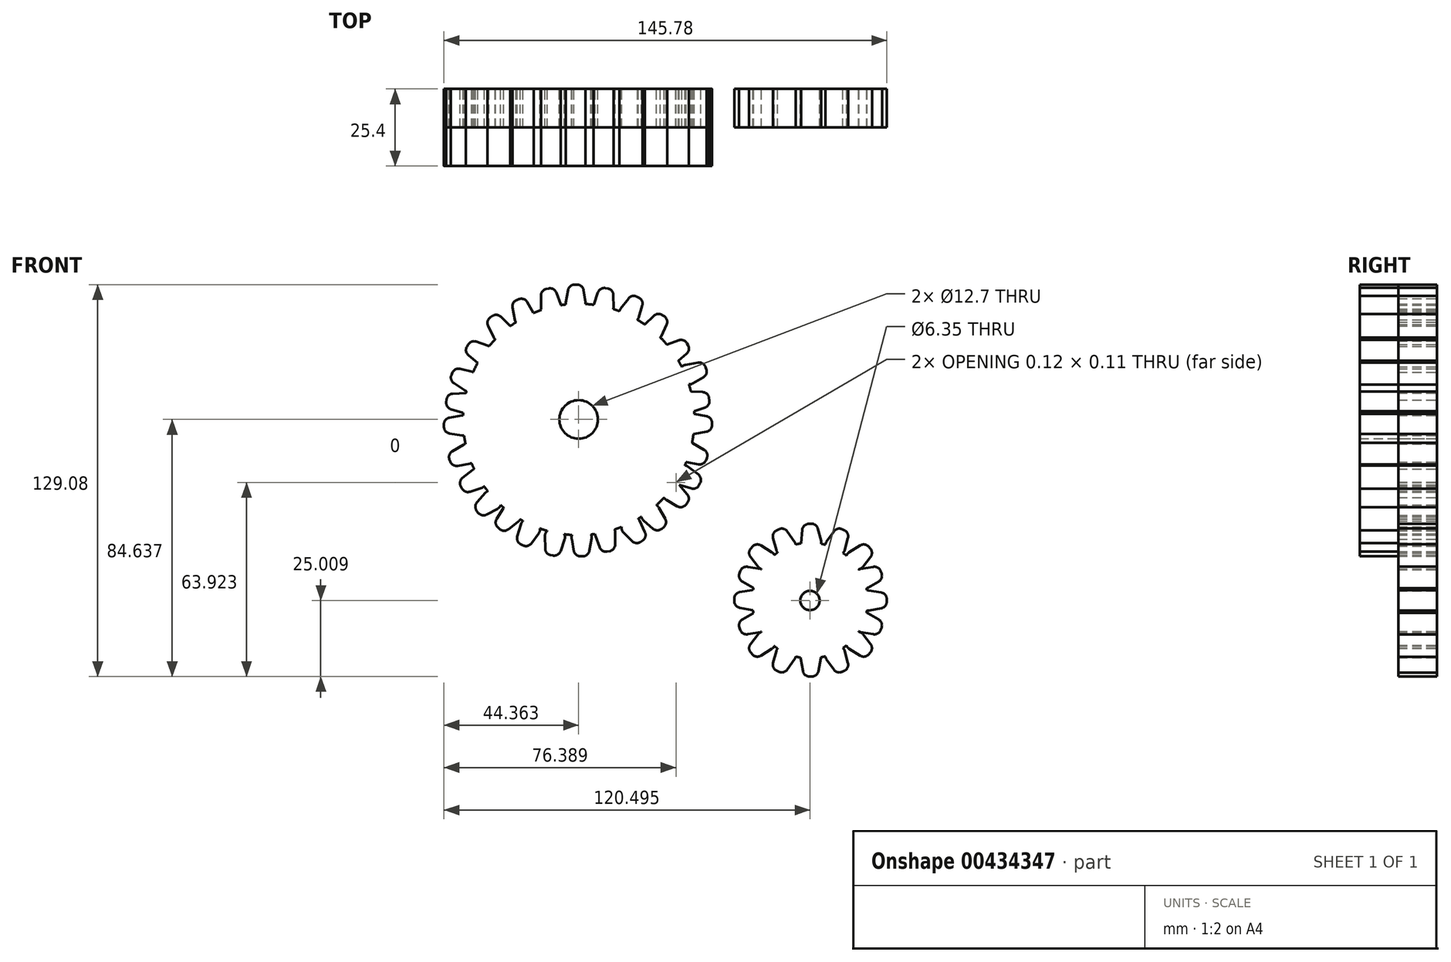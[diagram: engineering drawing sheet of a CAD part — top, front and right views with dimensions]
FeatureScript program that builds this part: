
annotation { "Feature Type Name" : "Feature", "Feature Type Description" : "" }
export const myFeature = defineFeature(function(context is Context, id is Id, definition is map)
    precondition{}
    {
        {
            var Q0;
            Q0=qCreatedBy(makeId("Front.planeOp"),FACE);
            var sketch = newSketch(context, id + "F0", { "sketchPlane" : qUnion([Q0])});
            skCircle(sketch, "E0", {"center": v(-37.42, 28.38) * mm, "radius": 38.1 * mm});
            skCircle(sketch, "E1", {"center": v(-37.42, 28.38) * mm, "radius": 6.35 * mm});
            skCircle(sketch, "E2", {"center": v(38.71, -31.25) * mm, "radius": 19.05 * mm});
            skCircle(sketch, "E3", {"center": v(38.71, -31.25) * mm, "radius": 3.18 * mm});
            skLineSegment(sketch, "E4", {"start": v(-40.93, 71.01) * mm, "end": v(-41.64, 66.96) * mm});
            skLineSegment(sketch, "E5", {"start": v(-38.77, 72.82) * mm, "end": v(-37.94, 72.82) * mm});
            skLineSegment(sketch, "E6", {"start": v(-39.65, 64.59) * mm, "end": v(-37.3, 64.59) * mm});
            skLineSegment(sketch, "E7", {"start": v(-35.15, 67.1) * mm, "end": v(-35.78, 70.98) * mm});
            skArc(sketch, "E8.filletArc", {"start": v(-35.78, 70.98) * mm, "mid": v(-36.52, 72.3) * mm, "end": v(-37.94, 72.82) * mm});
            skArc(sketch, "E9.filletArc", {"start": v(-38.77, 72.82) * mm, "mid": v(-40.18, 72.3) * mm, "end": v(-40.93, 71.01) * mm});
            skArc(sketch, "E10.filletArc", {"start": v(-41.64, 66.96) * mm, "mid": v(-41.2, 65.31) * mm, "end": v(-39.65, 64.59) * mm});
            skArc(sketch, "E11.filletArc", {"start": v(-37.3, 64.59) * mm, "mid": v(-35.64, 65.35) * mm, "end": v(-35.15, 67.1) * mm});
            skLineSegment(sketch, "E12", {"start": v(-31.09, 70.22) * mm, "end": v(-32.46, 66.35) * mm});
            skLineSegment(sketch, "E13", {"start": v(-28.66, 71.65) * mm, "end": v(-27.84, 71.52) * mm});
            skLineSegment(sketch, "E14", {"start": v(-30.88, 63.67) * mm, "end": v(-28.33, 63.25) * mm});
            skLineSegment(sketch, "E15", {"start": v(-25.97, 65.27) * mm, "end": v(-26.01, 69.38) * mm});
            skArc(sketch, "E16.filletArc", {"start": v(-26.01, 69.38) * mm, "mid": v(-26.54, 70.78) * mm, "end": v(-27.84, 71.52) * mm});
            skArc(sketch, "E17.filletArc", {"start": v(-28.66, 71.65) * mm, "mid": v(-30.13, 71.38) * mm, "end": v(-31.09, 70.22) * mm});
            skArc(sketch, "E18.filletArc", {"start": v(-32.46, 66.35) * mm, "mid": v(-32.29, 64.64) * mm, "end": v(-30.88, 63.67) * mm});
            skArc(sketch, "E19.filletArc", {"start": v(-28.33, 63.25) * mm, "mid": v(-26.68, 63.7) * mm, "end": v(-25.97, 65.27) * mm});
            skLineSegment(sketch, "E20", {"start": v(-12.7, 62.53) * mm, "end": v(-15.6, 59.62) * mm});
            skLineSegment(sketch, "E21", {"start": v(-9.9, 62.77) * mm, "end": v(-9.21, 62.3) * mm});
            skLineSegment(sketch, "E22", {"start": v(-15.33, 56.53) * mm, "end": v(-13.22, 55.05) * mm});
            skLineSegment(sketch, "E23", {"start": v(-10.22, 55.85) * mm, "end": v(-8.48, 59.58) * mm});
            skArc(sketch, "E24.filletArc", {"start": v(-8.48, 59.58) * mm, "mid": v(-8.35, 61.07) * mm, "end": v(-9.21, 62.3) * mm});
            skArc(sketch, "E25.filletArc", {"start": v(-9.9, 62.77) * mm, "mid": v(-11.34, 63.16) * mm, "end": v(-12.7, 62.53) * mm});
            skArc(sketch, "E26.filletArc", {"start": v(-15.6, 59.62) * mm, "mid": v(-16.19, 58.01) * mm, "end": v(-15.33, 56.53) * mm});
            skArc(sketch, "E27.filletArc", {"start": v(-13.22, 55.05) * mm, "mid": v(-11.53, 54.75) * mm, "end": v(-10.22, 55.85) * mm});
            skLineSegment(sketch, "E28", {"start": v(-4.46, 54.46) * mm, "end": v(-8.32, 53.05) * mm});
            skLineSegment(sketch, "E29", {"start": v(-1.81, 53.5) * mm, "end": v(-1.4, 52.78) * mm});
            skLineSegment(sketch, "E30", {"start": v(-9.38, 50.14) * mm, "end": v(-8.1, 47.9) * mm});
            skLineSegment(sketch, "E31", {"start": v(-5.04, 47.36) * mm, "end": v(-1.89, 50) * mm});
            skArc(sketch, "E32.filletArc", {"start": v(-1.89, 50) * mm, "mid": v(-1.14, 51.3) * mm, "end": v(-1.4, 52.78) * mm});
            skArc(sketch, "E33.filletArc", {"start": v(-1.81, 53.5) * mm, "mid": v(-2.96, 54.46) * mm, "end": v(-4.46, 54.46) * mm});
            skArc(sketch, "E34.filletArc", {"start": v(-8.32, 53.05) * mm, "mid": v(-9.53, 51.84) * mm, "end": v(-9.38, 50.14) * mm});
            skArc(sketch, "E35.filletArc", {"start": v(-8.1, 47.9) * mm, "mid": v(-6.7, 46.92) * mm, "end": v(-5.04, 47.36) * mm});
            skLineSegment(sketch, "E36", {"start": v(-33.88, -14.86) * mm, "end": v(-33.16, -10.81) * mm});
            skLineSegment(sketch, "E37", {"start": v(-36.03, -16.67) * mm, "end": v(-36.86, -16.67) * mm});
            skLineSegment(sketch, "E38", {"start": v(-35.16, -8.44) * mm, "end": v(-37.74, -8.44) * mm});
            skArc(sketch, "E39.filletArc", {"start": v(-38.95, -15.15) * mm, "mid": v(-38.16, -16.25) * mm, "end": v(-36.86, -16.67) * mm});
            skArc(sketch, "E40.filletArc", {"start": v(-36.03, -16.67) * mm, "mid": v(-34.63, -16.16) * mm, "end": v(-33.88, -14.86) * mm});
            skArc(sketch, "E41.filletArc", {"start": v(-33.16, -10.81) * mm, "mid": v(-33.6, -9.16) * mm, "end": v(-35.16, -8.44) * mm});
            skArc(sketch, "E42.filletArc", {"start": v(-37.74, -8.44) * mm, "mid": v(-39.38, -9.27) * mm, "end": v(-39.67, -11.09) * mm});
            skLineSegment(sketch, "E43", {"start": v(4.66, 29.47) * mm, "end": v(0.45, 30.2) * mm});
            skLineSegment(sketch, "E44", {"start": v(6.47, 27.3) * mm, "end": v(6.47, 26.48) * mm});
            skLineSegment(sketch, "E45", {"start": v(-1.8, 28.32) * mm, "end": v(-1.8, 25.63) * mm});
            skLineSegment(sketch, "E46", {"start": v(0.61, 23.6) * mm, "end": v(4.66, 24.32) * mm});
            skArc(sketch, "E47.filletArc", {"start": v(4.66, 24.32) * mm, "mid": v(5.96, 25.07) * mm, "end": v(6.47, 26.48) * mm});
            skArc(sketch, "E48.filletArc", {"start": v(6.47, 27.3) * mm, "mid": v(5.96, 28.72) * mm, "end": v(4.66, 29.47) * mm});
            skArc(sketch, "E49.filletArc", {"start": v(0.45, 30.2) * mm, "mid": v(-1.11, 29.79) * mm, "end": v(-1.8, 28.32) * mm});
            skArc(sketch, "E50.filletArc", {"start": v(-1.8, 25.63) * mm, "mid": v(-1.06, 24.06) * mm, "end": v(0.61, 23.6) * mm});
            skArc(sketch, "E51.filletArc", {"start": v(-76.25, 28.75) * mm, "mid": v(-76.3, 29.19) * mm, "end": v(-76.43, 29.6) * mm});
            skLineSegment(sketch, "E52", {"start": v(3.4, 37.4) * mm, "end": v(-0.87, 37.55) * mm});
            skLineSegment(sketch, "E53", {"start": v(5.49, 35.51) * mm, "end": v(5.6, 34.7) * mm});
            skLineSegment(sketch, "E54", {"start": v(-2.84, 35.38) * mm, "end": v(-2.47, 32.7) * mm});
            skLineSegment(sketch, "E55", {"start": v(0.2, 31.04) * mm, "end": v(4.1, 32.3) * mm});
            skArc(sketch, "E56.filletArc", {"start": v(4.1, 32.3) * mm, "mid": v(5.29, 33.23) * mm, "end": v(5.6, 34.7) * mm});
            skArc(sketch, "E57.filletArc", {"start": v(5.49, 35.51) * mm, "mid": v(4.78, 36.84) * mm, "end": v(3.4, 37.4) * mm});
            skArc(sketch, "E58.filletArc", {"start": v(-0.87, 37.55) * mm, "mid": v(-2.37, 36.92) * mm, "end": v(-2.84, 35.38) * mm});
            skArc(sketch, "E59.filletArc", {"start": v(-2.47, 32.7) * mm, "mid": v(-1.53, 31.25) * mm, "end": v(0.2, 31.04) * mm});
            skLineSegment(sketch, "E60", {"start": v(3.84, 18.44) * mm, "end": v(0.14, 20.58) * mm});
            skLineSegment(sketch, "E61", {"start": v(4.8, 15.8) * mm, "end": v(4.52, 15.02) * mm});
            skLineSegment(sketch, "E62", {"start": v(-2.62, 19.57) * mm, "end": v(-3.54, 17.04) * mm});
            skLineSegment(sketch, "E63", {"start": v(-1.97, 14.32) * mm, "end": v(2.08, 13.6) * mm});
            skArc(sketch, "E64.filletArc", {"start": v(2.08, 13.6) * mm, "mid": v(3.55, 13.87) * mm, "end": v(4.52, 15.02) * mm});
            skArc(sketch, "E65.filletArc", {"start": v(4.8, 15.8) * mm, "mid": v(4.8, 17.3) * mm, "end": v(3.84, 18.44) * mm});
            skArc(sketch, "E66.filletArc", {"start": v(0.14, 20.58) * mm, "mid": v(-1.48, 20.72) * mm, "end": v(-2.62, 19.57) * mm});
            skArc(sketch, "E67.filletArc", {"start": v(-3.54, 17.04) * mm, "mid": v(-3.4, 15.32) * mm, "end": v(-1.97, 14.32) * mm});
            skLineSegment(sketch, "E68", {"start": v(1.98, 10.22) * mm, "end": v(-1.4, 12.83) * mm});
            skLineSegment(sketch, "E69", {"start": v(2.58, 7.47) * mm, "end": v(2.2, 6.74) * mm});
            skLineSegment(sketch, "E70", {"start": v(-4.28, 12.2) * mm, "end": v(-5.52, 9.81) * mm});
            skLineSegment(sketch, "E71", {"start": v(-4.33, 6.9) * mm, "end": v(-0.4, 5.67) * mm});
            skArc(sketch, "E72.filletArc", {"start": v(-0.4, 5.67) * mm, "mid": v(1.1, 5.73) * mm, "end": v(2.2, 6.74) * mm});
            skArc(sketch, "E73.filletArc", {"start": v(2.58, 7.47) * mm, "mid": v(2.78, 8.96) * mm, "end": v(1.98, 10.22) * mm});
            skArc(sketch, "E74.filletArc", {"start": v(-1.4, 12.83) * mm, "mid": v(-2.99, 13.18) * mm, "end": v(-4.28, 12.2) * mm});
            skArc(sketch, "E75.filletArc", {"start": v(-5.52, 9.81) * mm, "mid": v(-5.6, 8.08) * mm, "end": v(-4.33, 6.9) * mm});
            skLineSegment(sketch, "E76.MirrorCS", {"start": v(-48.45, -14.17) * mm, "end": v(-48.5, -9.9) * mm});
            skArc(sketch, "E77.MirrorCS", {"start": v(-76.23, 6.36) * mm, "mid": v(-76.44, 7.84) * mm, "end": v(-75.66, 9.11) * mm});
            skArc(sketch, "E78.MirrorCS", {"start": v(-70.95, -1.73) * mm, "mid": v(-71.42, -0.3) * mm, "end": v(-70.86, 1.1) * mm});
            skLineSegment(sketch, "E79.MirrorCS", {"start": v(-70.95, -1.73) * mm, "end": v(-70.43, -2.37) * mm});
            skArc(sketch, "E80.MirrorCS", {"start": v(-68.02, 4.28) * mm, "mid": v(-66.54, 4.92) * mm, "end": v(-65.09, 4.2) * mm});
            skArc(sketch, "E81.MirrorCS", {"start": v(-51.3, -6.08) * mm, "mid": v(-50.22, -7.44) * mm, "end": v(-50.57, -9.14) * mm});
            skArc(sketch, "E82.MirrorCS", {"start": v(-73.21, 4.59) * mm, "mid": v(-74.71, 4.63) * mm, "end": v(-75.83, 5.63) * mm});
            skLineSegment(sketch, "E83.MirrorCS", {"start": v(-75.66, 9.11) * mm, "end": v(-72.3, 11.76) * mm});
            skLineSegment(sketch, "E84.MirrorCS", {"start": v(-70.86, 1.1) * mm, "end": v(-68.02, 4.28) * mm});
            skLineSegment(sketch, "E85.MirrorCS", {"start": v(-64.06, -1) * mm, "end": v(-67.68, -2.94) * mm});
            skArc(sketch, "E86.MirrorCS", {"start": v(-56.4, -6.05) * mm, "mid": v(-55.33, -4.83) * mm, "end": v(-53.71, -4.88) * mm});
            skArc(sketch, "E87.MirrorCS", {"start": v(-48.5, -9.9) * mm, "mid": v(-47.84, -8.42) * mm, "end": v(-46.28, -7.99) * mm});
            skLineSegment(sketch, "E88.MirrorCS", {"start": v(-76.23, 6.36) * mm, "end": v(-75.83, 5.63) * mm});
            skLineSegment(sketch, "E89.MirrorCS", {"start": v(-56.5, -12.73) * mm, "end": v(-55.76, -13.1) * mm});
            skLineSegment(sketch, "E90.MirrorCS", {"start": v(-57.62, -10.14) * mm, "end": v(-56.4, -6.05) * mm});
            skLineSegment(sketch, "E91.MirrorCS", {"start": v(-73.17, 13.87) * mm, "end": v(-77.2, 13.1) * mm});
            skArc(sketch, "E92.MirrorCS", {"start": v(-63.42, 2.08) * mm, "mid": v(-63.02, 0.4) * mm, "end": v(-64.06, -1) * mm});
            skLineSegment(sketch, "E93.MirrorCS", {"start": v(-65.09, 4.2) * mm, "end": v(-63.42, 2.08) * mm});
            skLineSegment(sketch, "E94.MirrorCS", {"start": v(-50.57, -9.14) * mm, "end": v(-53.02, -12.44) * mm});
            skLineSegment(sketch, "E95.MirrorCS", {"start": v(-53.71, -4.88) * mm, "end": v(-51.3, -6.08) * mm});
            skArc(sketch, "E96.MirrorCS", {"start": v(-68.15, 8.8) * mm, "mid": v(-68.05, 7.07) * mm, "end": v(-69.31, 5.88) * mm});
            skArc(sketch, "E97.MirrorCS", {"start": v(-72.3, 11.76) * mm, "mid": v(-70.73, 12.14) * mm, "end": v(-69.43, 11.17) * mm});
            skLineSegment(sketch, "E98.MirrorCS", {"start": v(-69.43, 11.17) * mm, "end": v(-68.15, 8.8) * mm});
            skLineSegment(sketch, "E99.MirrorCS", {"start": v(-69.31, 5.88) * mm, "end": v(-73.21, 4.59) * mm});
            skArc(sketch, "E100.MirrorCS", {"start": v(-53.02, -12.44) * mm, "mid": v(-54.27, -13.27) * mm, "end": v(-55.76, -13.1) * mm});
            skLineSegment(sketch, "E101.MirrorCS", {"start": v(-46.28, -7.99) * mm, "end": v(-43.62, -8.42) * mm});
            skArc(sketch, "E102.MirrorCS", {"start": v(-56.5, -12.73) * mm, "mid": v(-57.53, -11.64) * mm, "end": v(-57.62, -10.14) * mm});
            skArc(sketch, "E103.MirrorCS", {"start": v(-67.68, -2.94) * mm, "mid": v(-69.16, -3.16) * mm, "end": v(-70.43, -2.37) * mm});
            skArc(sketch, "E104.MirrorCS", {"start": v(-71.63, 16.6) * mm, "mid": v(-71.76, 14.88) * mm, "end": v(-73.17, 13.87) * mm});
            skLineSegment(sketch, "E105.MirrorCS", {"start": v(-57.05, 68) * mm, "end": v(-57.82, 67.72) * mm});
            skArc(sketch, "E106.MirrorCS", {"start": v(-75.8, 29.72) * mm, "mid": v(-74.23, 29.32) * mm, "end": v(-73.52, 27.87) * mm});
            skLineSegment(sketch, "E107.MirrorCS", {"start": v(-78.95, 43.83) * mm, "end": v(-79.3, 43.08) * mm});
            skArc(sketch, "E108.MirrorCS", {"start": v(-43.62, -8.42) * mm, "mid": v(-42.19, -9.4) * mm, "end": v(-42.02, -11.12) * mm});
            skArc(sketch, "E109.MirrorCS", {"start": v(-79.47, 31.77) * mm, "mid": v(-80.67, 32.68) * mm, "end": v(-81, 34.14) * mm});
            skArc(sketch, "E110.MirrorCS", {"start": v(-47.44, 63.13) * mm, "mid": v(-49.09, 63.57) * mm, "end": v(-49.82, 65.12) * mm});
            skArc(sketch, "E111.MirrorCS", {"start": v(-62.44, 54.73) * mm, "mid": v(-64.12, 54.42) * mm, "end": v(-65.45, 55.5) * mm});
            skLineSegment(sketch, "E112.MirrorCS", {"start": v(-75.55, 30.56) * mm, "end": v(-79.47, 31.77) * mm});
            skLineSegment(sketch, "E113.MirrorCS", {"start": v(-47.21, 71.54) * mm, "end": v(-48.03, 71.39) * mm});
            skLineSegment(sketch, "E114.MirrorCS", {"start": v(-65.87, 62.41) * mm, "end": v(-66.54, 61.93) * mm});
            skArc(sketch, "E115.MirrorCS", {"start": v(-43.37, -15) * mm, "mid": v(-44.32, -16.16) * mm, "end": v(-45.8, -16.44) * mm});
            skArc(sketch, "E116.MirrorCS", {"start": v(-77.2, 13.1) * mm, "mid": v(-78.69, 13.34) * mm, "end": v(-79.66, 14.48) * mm});
            skLineSegment(sketch, "E117.MirrorCS", {"start": v(-46.61, -16.3) * mm, "end": v(-45.8, -16.44) * mm});
            skLineSegment(sketch, "E118.MirrorCS", {"start": v(-73.82, 53.04) * mm, "end": v(-74.23, 52.32) * mm});
            skLineSegment(sketch, "E119.MirrorCS", {"start": v(-81.78, 26.75) * mm, "end": v(-81.77, 25.92) * mm});
            skArc(sketch, "E120.MirrorCS", {"start": v(-49.83, 69.23) * mm, "mid": v(-49.32, 70.64) * mm, "end": v(-48.03, 71.39) * mm});
            skArc(sketch, "E121.MirrorCS", {"start": v(-67.23, 59.2) * mm, "mid": v(-67.38, 60.7) * mm, "end": v(-66.54, 61.93) * mm});
            skArc(sketch, "E122.MirrorCS", {"start": v(-74.56, 37.09) * mm, "mid": v(-73.06, 36.47) * mm, "end": v(-72.57, 34.93) * mm});
            skArc(sketch, "E123.MirrorCS", {"start": v(-65.87, 62.41) * mm, "mid": v(-64.42, 62.82) * mm, "end": v(-63.06, 62.2) * mm});
            skLineSegment(sketch, "E124.MirrorCS", {"start": v(-72.57, 34.93) * mm, "end": v(-72.9, 32.26) * mm});
            skArc(sketch, "E125.MirrorCS", {"start": v(-46.61, -16.3) * mm, "mid": v(-47.92, -15.57) * mm, "end": v(-48.45, -14.17) * mm});
            skLineSegment(sketch, "E126.MirrorCS", {"start": v(-71, 41.36) * mm, "end": v(-72.1, 38.9) * mm});
            skLineSegment(sketch, "E127.MirrorCS", {"start": v(-73.52, 27.87) * mm, "end": v(-73.49, 25.17) * mm});
            skLineSegment(sketch, "E128.MirrorCS", {"start": v(-66.21, 49.78) * mm, "end": v(-67.47, 47.52) * mm});
            skLineSegment(sketch, "E129.MirrorCS", {"start": v(-53.31, 60.62) * mm, "end": v(-55.73, 59.7) * mm});
            skArc(sketch, "E130.MirrorCS", {"start": v(-72.9, 32.26) * mm, "mid": v(-73.83, 30.8) * mm, "end": v(-75.55, 30.56) * mm});
            skLineSegment(sketch, "E131.MirrorCS", {"start": v(-75.87, 23.12) * mm, "end": v(-79.93, 23.78) * mm});
            skLineSegment(sketch, "E132.MirrorCS", {"start": v(-70.52, 46.95) * mm, "end": v(-73.7, 49.55) * mm});
            skArc(sketch, "E133.MirrorCS", {"start": v(-60.11, 59.34) * mm, "mid": v(-59.5, 57.74) * mm, "end": v(-60.34, 56.24) * mm});
            skLineSegment(sketch, "E134.MirrorCS", {"start": v(-58.44, 61.22) * mm, "end": v(-59.2, 65.26) * mm});
            skLineSegment(sketch, "E135.MirrorCS", {"start": v(-75.13, 38.05) * mm, "end": v(-78.53, 40.37) * mm});
            skArc(sketch, "E136.MirrorCS", {"start": v(-67.3, 52.68) * mm, "mid": v(-66.08, 51.48) * mm, "end": v(-66.21, 49.78) * mm});
            skArc(sketch, "E137.MirrorCS", {"start": v(-52.29, 63.55) * mm, "mid": v(-52.12, 61.84) * mm, "end": v(-53.31, 60.62) * mm});
            skLineSegment(sketch, "E138.MirrorCS", {"start": v(-72.58, 19.13) * mm, "end": v(-71.63, 16.6) * mm});
            skLineSegment(sketch, "E139.MirrorCS", {"start": v(-65.45, 55.5) * mm, "end": v(-67.23, 59.2) * mm});
            skArc(sketch, "E140.MirrorCS", {"start": v(-43.35, 66.28) * mm, "mid": v(-43.5, 64.57) * mm, "end": v(-44.9, 63.58) * mm});
            skArc(sketch, "E141.MirrorCS", {"start": v(-73.82, 53.04) * mm, "mid": v(-72.69, 54.02) * mm, "end": v(-71.19, 54.03) * mm});
            skLineSegment(sketch, "E142.MirrorCS", {"start": v(-49.82, 65.12) * mm, "end": v(-49.83, 69.23) * mm});
            skArc(sketch, "E143.MirrorCS", {"start": v(-73.7, 49.55) * mm, "mid": v(-74.47, 50.84) * mm, "end": v(-74.23, 52.32) * mm});
            skArc(sketch, "E144.MirrorCS", {"start": v(-57.05, 68) * mm, "mid": v(-55.55, 68.03) * mm, "end": v(-54.39, 67.08) * mm});
            skArc(sketch, "E145.MirrorCS", {"start": v(-81.78, 26.75) * mm, "mid": v(-81.28, 28.16) * mm, "end": v(-80, 28.93) * mm});
            skArc(sketch, "E146.MirrorCS", {"start": v(-55.73, 59.7) * mm, "mid": v(-57.44, 59.83) * mm, "end": v(-58.44, 61.22) * mm});
            skArc(sketch, "E147.MirrorCS", {"start": v(-80.9, 34.96) * mm, "mid": v(-80.2, 36.3) * mm, "end": v(-78.83, 36.88) * mm});
            skLineSegment(sketch, "E148.MirrorCS", {"start": v(-80, 28.93) * mm, "end": v(-75.8, 29.72) * mm});
            skLineSegment(sketch, "E149.MirrorCS", {"start": v(-76.41, 45.06) * mm, "end": v(-72.27, 44) * mm});
            skArc(sketch, "E150.MirrorCS", {"start": v(-72.27, 44) * mm, "mid": v(-71.02, 42.98) * mm, "end": v(-71, 41.36) * mm});
            skArc(sketch, "E151.MirrorCS", {"start": v(-79.93, 23.78) * mm, "mid": v(-81.23, 24.52) * mm, "end": v(-81.77, 25.92) * mm});
            skLineSegment(sketch, "E152.MirrorCS", {"start": v(-44.9, 63.58) * mm, "end": v(-47.44, 63.13) * mm});
            skArc(sketch, "E153.MirrorCS", {"start": v(-78.53, 40.37) * mm, "mid": v(-79.4, 41.58) * mm, "end": v(-79.3, 43.08) * mm});
            skLineSegment(sketch, "E154.MirrorCS", {"start": v(-44.77, 70.13) * mm, "end": v(-43.35, 66.28) * mm});
            skLineSegment(sketch, "E155.MirrorCS", {"start": v(-60.34, 56.24) * mm, "end": v(-62.44, 54.73) * mm});
            skArc(sketch, "E156.MirrorCS", {"start": v(-79.96, 15.25) * mm, "mid": v(-79.98, 16.75) * mm, "end": v(-79.03, 17.91) * mm});
            skLineSegment(sketch, "E157.MirrorCS", {"start": v(-79.96, 15.25) * mm, "end": v(-79.66, 14.48) * mm});
            skLineSegment(sketch, "E158.MirrorCS", {"start": v(-78.83, 36.88) * mm, "end": v(-74.56, 37.09) * mm});
            skLineSegment(sketch, "E159.MirrorCS", {"start": v(-63.06, 62.2) * mm, "end": v(-60.11, 59.34) * mm});
            skLineSegment(sketch, "E160.MirrorCS", {"start": v(-79.03, 17.91) * mm, "end": v(-75.35, 20.1) * mm});
            skArc(sketch, "E161.MirrorCS", {"start": v(-67.47, 47.52) * mm, "mid": v(-68.86, 46.52) * mm, "end": v(-70.52, 46.95) * mm});
            skLineSegment(sketch, "E162.MirrorCS", {"start": v(-80.9, 34.96) * mm, "end": v(-81, 34.14) * mm});
            skArc(sketch, "E163.MirrorCS", {"start": v(-47.21, 71.54) * mm, "mid": v(-45.73, 71.28) * mm, "end": v(-44.77, 70.13) * mm});
            skLineSegment(sketch, "E164.MirrorCS", {"start": v(-42.02, -11.12) * mm, "end": v(-43.37, -15) * mm});
            skArc(sketch, "E165.MirrorCS", {"start": v(-75.35, 20.1) * mm, "mid": v(-73.74, 20.26) * mm, "end": v(-72.58, 19.13) * mm});
            skArc(sketch, "E166.MirrorCS", {"start": v(-78.95, 43.83) * mm, "mid": v(-77.9, 44.9) * mm, "end": v(-76.41, 45.06) * mm});
            skArc(sketch, "E167.MirrorCS", {"start": v(-73.49, 25.17) * mm, "mid": v(-74.2, 23.6) * mm, "end": v(-75.87, 23.12) * mm});
            skLineSegment(sketch, "E168.MirrorCS", {"start": v(-71.19, 54.03) * mm, "end": v(-67.3, 52.68) * mm});
            skLineSegment(sketch, "E169.MirrorCS", {"start": v(-54.39, 67.08) * mm, "end": v(-52.29, 63.55) * mm});
            skArc(sketch, "E170.MirrorCS", {"start": v(-72.1, 38.9) * mm, "mid": v(-73.42, 37.77) * mm, "end": v(-75.13, 38.05) * mm});
            skArc(sketch, "E171.MirrorCS", {"start": v(-59.2, 65.26) * mm, "mid": v(-58.96, 66.74) * mm, "end": v(-57.82, 67.72) * mm});
            skLineSegment(sketch, "E172", {"start": v(-15.6, -8.72) * mm, "end": v(-17.4, -4.85) * mm});
            skLineSegment(sketch, "E173", {"start": v(-16.32, -11.45) * mm, "end": v(-17, -11.92) * mm});
            skLineSegment(sketch, "E174", {"start": v(-20.23, -4.1) * mm, "end": v(-22.44, -5.64) * mm});
            skLineSegment(sketch, "E175", {"start": v(-22.71, -8.77) * mm, "end": v(-19.8, -11.67) * mm});
            skArc(sketch, "E176.filletArc", {"start": v(-19.8, -11.67) * mm, "mid": v(-18.45, -12.3) * mm, "end": v(-17, -11.92) * mm});
            skArc(sketch, "E177.filletArc", {"start": v(-16.32, -11.45) * mm, "mid": v(-15.46, -10.22) * mm, "end": v(-15.6, -8.72) * mm});
            skArc(sketch, "E178.filletArc", {"start": v(-17.4, -4.85) * mm, "mid": v(-18.64, -3.81) * mm, "end": v(-20.23, -4.1) * mm});
            skArc(sketch, "E179.filletArc", {"start": v(-22.44, -5.64) * mm, "mid": v(-23.3, -7.14) * mm, "end": v(-22.71, -8.77) * mm});
            skLineSegment(sketch, "E180", {"start": v(1.86, 47.1) * mm, "end": v(-2.35, 46.35) * mm});
            skLineSegment(sketch, "E181", {"start": v(4.3, 45.68) * mm, "end": v(4.58, 44.9) * mm});
            skLineSegment(sketch, "E182", {"start": v(-3.82, 43.8) * mm, "end": v(-2.9, 41.28) * mm});
            skLineSegment(sketch, "E183", {"start": v(0.06, 40.2) * mm, "end": v(3.62, 42.26) * mm});
            skArc(sketch, "E184.filletArc", {"start": v(3.62, 42.26) * mm, "mid": v(4.58, 43.4) * mm, "end": v(4.58, 44.9) * mm});
            skArc(sketch, "E185.filletArc", {"start": v(4.3, 45.68) * mm, "mid": v(3.33, 46.83) * mm, "end": v(1.86, 47.1) * mm});
            skArc(sketch, "E186.filletArc", {"start": v(-2.35, 46.35) * mm, "mid": v(-3.68, 45.42) * mm, "end": v(-3.82, 43.8) * mm});
            skArc(sketch, "E187.filletArc", {"start": v(-2.9, 41.28) * mm, "mid": v(-1.67, 40.05) * mm, "end": v(0.06, 40.2) * mm});
            skLineSegment(sketch, "E188", {"start": v(-1.66, 3.73) * mm, "end": v(-4.4, 7) * mm});
            skLineSegment(sketch, "E189", {"start": v(-1.66, 0.91) * mm, "end": v(-2.19, 0.28) * mm});
            skLineSegment(sketch, "E190", {"start": v(-7.34, 7) * mm, "end": v(-9.07, 4.94) * mm});
            skLineSegment(sketch, "E191", {"start": v(-8.52, 1.84) * mm, "end": v(-4.96, -0.21) * mm});
            skArc(sketch, "E192.filletArc", {"start": v(-4.96, -0.21) * mm, "mid": v(-3.49, -0.47) * mm, "end": v(-2.19, 0.28) * mm});
            skArc(sketch, "E193.filletArc", {"start": v(-1.66, 0.91) * mm, "mid": v(-1.14, 2.32) * mm, "end": v(-1.66, 3.73) * mm});
            skArc(sketch, "E194.filletArc", {"start": v(-4.4, 7) * mm, "mid": v(-5.87, 7.69) * mm, "end": v(-7.34, 7) * mm});
            skArc(sketch, "E195.filletArc", {"start": v(-9.07, 4.94) * mm, "mid": v(-9.52, 3.27) * mm, "end": v(-8.52, 1.84) * mm});
            skLineSegment(sketch, "E196", {"start": v(-8.95, -4.3) * mm, "end": v(-11.07, -0.6) * mm});
            skLineSegment(sketch, "E197", {"start": v(-9.46, -7.08) * mm, "end": v(-10.1, -7.6) * mm});
            skLineSegment(sketch, "E198", {"start": v(-13.95, -0.07) * mm, "end": v(-16.03, -1.79) * mm});
            skLineSegment(sketch, "E199", {"start": v(-16.04, -4.93) * mm, "end": v(-12.91, -7.6) * mm});
            skArc(sketch, "E200.filletArc", {"start": v(-12.91, -7.6) * mm, "mid": v(-11.5, -8.11) * mm, "end": v(-10.1, -7.6) * mm});
            skArc(sketch, "E201.filletArc", {"start": v(-9.46, -7.08) * mm, "mid": v(-8.7, -5.79) * mm, "end": v(-8.95, -4.3) * mm});
            skArc(sketch, "E202.filletArc", {"start": v(-11.07, -0.6) * mm, "mid": v(-12.39, 0.34) * mm, "end": v(-13.95, -0.07) * mm});
            skArc(sketch, "E203.filletArc", {"start": v(-16.03, -1.79) * mm, "mid": v(-16.77, -3.36) * mm, "end": v(-16.04, -4.93) * mm});
            skLineSegment(sketch, "E204", {"start": v(-25.43, -12.84) * mm, "end": v(-25.43, -8.56) * mm});
            skLineSegment(sketch, "E205", {"start": v(-27.24, -15) * mm, "end": v(-28.06, -15.14) * mm});
            skLineSegment(sketch, "E206", {"start": v(-27.68, -6.68) * mm, "end": v(-30.33, -7.14) * mm});
            skLineSegment(sketch, "E207", {"start": v(-31.9, -9.87) * mm, "end": v(-30.5, -13.73) * mm});
            skArc(sketch, "E208.filletArc", {"start": v(-30.5, -13.73) * mm, "mid": v(-29.53, -14.88) * mm, "end": v(-28.06, -15.14) * mm});
            skArc(sketch, "E209.filletArc", {"start": v(-27.24, -15) * mm, "mid": v(-25.95, -14.24) * mm, "end": v(-25.43, -12.84) * mm});
            skArc(sketch, "E210.filletArc", {"start": v(-25.43, -8.56) * mm, "mid": v(-26.12, -7.1) * mm, "end": v(-27.68, -6.68) * mm});
            skArc(sketch, "E211.filletArc", {"start": v(-30.33, -7.14) * mm, "mid": v(-31.75, -8.14) * mm, "end": v(-31.9, -9.87) * mm});
            skLineSegment(sketch, "E212", {"start": v(-38.95, -15.15) * mm, "end": v(-39.67, -11.09) * mm});
            skLineSegment(sketch, "E213", {"start": v(-60.59, -7.83) * mm, "end": v(-57.22, -5.2) * mm});
            skLineSegment(sketch, "E214", {"start": v(-63.4, -7.73) * mm, "end": v(-64.02, -7.18) * mm});
            skLineSegment(sketch, "E215", {"start": v(-57.11, -2.27) * mm, "end": v(-59.11, -0.47) * mm});
            skLineSegment(sketch, "E216", {"start": v(-62.23, -0.9) * mm, "end": v(-64.4, -4.39) * mm});
            skArc(sketch, "E217.filletArc", {"start": v(-64.4, -4.39) * mm, "mid": v(-64.72, -5.85) * mm, "end": v(-64.02, -7.18) * mm});
            skArc(sketch, "E218.filletArc", {"start": v(-63.4, -7.73) * mm, "mid": v(-62.01, -8.3) * mm, "end": v(-60.59, -7.83) * mm});
            skArc(sketch, "E219.filletArc", {"start": v(-57.22, -5.2) * mm, "mid": v(-56.48, -3.76) * mm, "end": v(-57.11, -2.27) * mm});
            skArc(sketch, "E220.filletArc", {"start": v(-59.11, -0.47) * mm, "mid": v(-60.77, 0.04) * mm, "end": v(-62.23, -0.9) * mm});
            skLineSegment(sketch, "E221", {"start": v(67.67, -31.25) * mm, "end": v(13.37, -31.25) * mm});
            skLineSegment(sketch, "E222", {"start": v(46.57, -8.5) * mm, "end": v(44.12, -12) * mm});
            skLineSegment(sketch, "E223", {"start": v(49.29, -7.76) * mm, "end": v(50.04, -8.11) * mm});
            skLineSegment(sketch, "E224", {"start": v(44.87, -14.83) * mm, "end": v(47.31, -15.97) * mm});
            skLineSegment(sketch, "E225", {"start": v(50.16, -14.64) * mm, "end": v(51.23, -10.67) * mm});
            skArc(sketch, "E226.filletArc", {"start": v(51.23, -10.67) * mm, "mid": v(51.1, -9.17) * mm, "end": v(50.04, -8.11) * mm});
            skArc(sketch, "E227.filletArc", {"start": v(49.29, -7.76) * mm, "mid": v(47.8, -7.63) * mm, "end": v(46.57, -8.5) * mm});
            skArc(sketch, "E228.filletArc", {"start": v(44.12, -12) * mm, "mid": v(43.83, -13.59) * mm, "end": v(44.87, -14.83) * mm});
            skArc(sketch, "E229.filletArc", {"start": v(47.31, -15.97) * mm, "mid": v(49.05, -15.97) * mm, "end": v(50.16, -14.64) * mm});
            skLineSegment(sketch, "E230", {"start": v(55.2, -13.1) * mm, "end": v(51.59, -15.36) * mm});
            skLineSegment(sketch, "E231", {"start": v(58, -13.49) * mm, "end": v(58.55, -14.1) * mm});
            skLineSegment(sketch, "E232", {"start": v(51.18, -18.27) * mm, "end": v(52.98, -20.27) * mm});
            skLineSegment(sketch, "E233", {"start": v(56.12, -20.16) * mm, "end": v(58.65, -16.92) * mm});
            skArc(sketch, "E234.filletArc", {"start": v(58.65, -16.92) * mm, "mid": v(59.12, -15.5) * mm, "end": v(58.55, -14.1) * mm});
            skArc(sketch, "E235.filletArc", {"start": v(58, -13.49) * mm, "mid": v(56.68, -12.79) * mm, "end": v(55.2, -13.1) * mm});
            skArc(sketch, "E236.filletArc", {"start": v(51.59, -15.36) * mm, "mid": v(50.7, -16.72) * mm, "end": v(51.18, -18.27) * mm});
            skArc(sketch, "E237.filletArc", {"start": v(52.98, -20.27) * mm, "mid": v(54.58, -20.95) * mm, "end": v(56.12, -20.16) * mm});
            skLineSegment(sketch, "E238", {"start": v(35.3, -12.51) * mm, "end": v(35.27, -12.66) * mm});
            skArc(sketch, "E239.filletArc", {"start": v(38.9, -6.67) * mm, "mid": v(38.87, -6.67) * mm, "end": v(38.83, -6.67) * mm});
            skLineSegment(sketch, "E240", {"start": v(59.57, -20.14) * mm, "end": v(55.36, -20.88) * mm});
            skLineSegment(sketch, "E241", {"start": v(62, -21.55) * mm, "end": v(62.29, -22.33) * mm});
            skLineSegment(sketch, "E242", {"start": v(53.9, -23.43) * mm, "end": v(54.81, -25.95) * mm});
            skLineSegment(sketch, "E243", {"start": v(57.77, -27.03) * mm, "end": v(61.33, -24.98) * mm});
            skArc(sketch, "E244.filletArc", {"start": v(61.33, -24.98) * mm, "mid": v(62.29, -23.83) * mm, "end": v(62.29, -22.33) * mm});
            skArc(sketch, "E245.filletArc", {"start": v(62, -21.55) * mm, "mid": v(61.04, -20.4) * mm, "end": v(59.57, -20.14) * mm});
            skArc(sketch, "E246.filletArc", {"start": v(55.36, -20.88) * mm, "mid": v(54.03, -21.81) * mm, "end": v(53.9, -23.43) * mm});
            skArc(sketch, "E247.filletArc", {"start": v(54.81, -25.95) * mm, "mid": v(56.04, -27.18) * mm, "end": v(57.77, -27.03) * mm});
            skLineSegment(sketch, "E248.MirrorCS", {"start": v(19.8, -13.49) * mm, "end": v(19.25, -14.1) * mm});
            skLineSegment(sketch, "E249.MirrorCS", {"start": v(15.8, -21.55) * mm, "end": v(15.51, -22.33) * mm});
            skLineSegment(sketch, "E250.MirrorCS", {"start": v(26.62, -18.27) * mm, "end": v(24.82, -20.27) * mm});
            skLineSegment(sketch, "E251.MirrorCS", {"start": v(23.91, -23.43) * mm, "end": v(22.99, -25.95) * mm});
            skArc(sketch, "E252.MirrorCS", {"start": v(22.99, -25.95) * mm, "mid": v(21.76, -27.18) * mm, "end": v(20.04, -27.03) * mm});
            skArc(sketch, "E253.MirrorCS", {"start": v(19.15, -16.92) * mm, "mid": v(18.69, -15.5) * mm, "end": v(19.25, -14.1) * mm});
            skArc(sketch, "E254.MirrorCS", {"start": v(16.48, -24.98) * mm, "mid": v(15.51, -23.83) * mm, "end": v(15.51, -22.33) * mm});
            skArc(sketch, "E255.MirrorCS", {"start": v(26.21, -15.36) * mm, "mid": v(27.1, -16.72) * mm, "end": v(26.62, -18.27) * mm});
            skLineSegment(sketch, "E256.MirrorCS", {"start": v(28.52, -7.76) * mm, "end": v(27.76, -8.11) * mm});
            skLineSegment(sketch, "E257.MirrorCS", {"start": v(32.93, -14.83) * mm, "end": v(30.49, -15.97) * mm});
            skLineSegment(sketch, "E258.MirrorCS", {"start": v(21.68, -20.16) * mm, "end": v(19.15, -16.92) * mm});
            skLineSegment(sketch, "E259.MirrorCS", {"start": v(20.04, -27.03) * mm, "end": v(16.48, -24.98) * mm});
            skArc(sketch, "E260.MirrorCS", {"start": v(24.82, -20.27) * mm, "mid": v(23.22, -20.95) * mm, "end": v(21.68, -20.16) * mm});
            skArc(sketch, "E261.MirrorCS", {"start": v(19.8, -13.49) * mm, "mid": v(21.13, -12.79) * mm, "end": v(22.6, -13.1) * mm});
            skArc(sketch, "E262.MirrorCS", {"start": v(15.8, -21.55) * mm, "mid": v(16.76, -20.4) * mm, "end": v(18.24, -20.14) * mm});
            skArc(sketch, "E263.MirrorCS", {"start": v(22.44, -20.88) * mm, "mid": v(23.77, -21.81) * mm, "end": v(23.91, -23.43) * mm});
            skLineSegment(sketch, "E264.MirrorCS", {"start": v(27.64, -14.64) * mm, "end": v(26.57, -10.67) * mm});
            skArc(sketch, "E265.MirrorCS", {"start": v(26.57, -10.67) * mm, "mid": v(26.7, -9.17) * mm, "end": v(27.76, -8.11) * mm});
            skArc(sketch, "E266.MirrorCS", {"start": v(28.52, -7.76) * mm, "mid": v(30, -7.63) * mm, "end": v(31.24, -8.5) * mm});
            skArc(sketch, "E267.MirrorCS", {"start": v(30.49, -15.97) * mm, "mid": v(28.75, -15.97) * mm, "end": v(27.64, -14.64) * mm});
            skLineSegment(sketch, "E268.MirrorCS", {"start": v(18.24, -20.14) * mm, "end": v(22.44, -20.88) * mm});
            skLineSegment(sketch, "E269.MirrorCS", {"start": v(22.6, -13.1) * mm, "end": v(26.21, -15.36) * mm});
            skLineSegment(sketch, "E270.MirrorCS", {"start": v(31.24, -8.5) * mm, "end": v(33.69, -12) * mm});
            skArc(sketch, "E271.MirrorCS", {"start": v(33.69, -12) * mm, "mid": v(33.97, -13.59) * mm, "end": v(32.93, -14.83) * mm});
            skLineSegment(sketch, "E272.MirrorCS", {"start": v(38.9, -15.06) * mm, "end": v(38.25, -15.06) * mm});
            skArc(sketch, "E273.MirrorCS", {"start": v(38.9, -6.67) * mm, "mid": v(38.93, -6.67) * mm, "end": v(38.97, -6.67) * mm});
            skLineSegment(sketch, "E274.MirrorCS", {"start": v(36.1, -12.5) * mm, "end": v(36.12, -12.38) * mm});
            skLineSegment(sketch, "E275.MirrorCS", {"start": v(42.52, -12.59) * mm, "end": v(42.53, -12.66) * mm});
            skLineSegment(sketch, "E276.MirrorCS", {"start": v(44.87, -47.67) * mm, "end": v(47.31, -46.54) * mm});
            skLineSegment(sketch, "E277.MirrorCS", {"start": v(58, -49.01) * mm, "end": v(58.55, -48.4) * mm});
            skLineSegment(sketch, "E278.MirrorCS", {"start": v(26.62, -44.23) * mm, "end": v(24.82, -42.23) * mm});
            skLineSegment(sketch, "E279.MirrorCS", {"start": v(49.29, -54.74) * mm, "end": v(50.04, -54.39) * mm});
            skLineSegment(sketch, "E280.MirrorCS", {"start": v(32.93, -47.67) * mm, "end": v(30.49, -46.54) * mm});
            skLineSegment(sketch, "E281.MirrorCS", {"start": v(28.52, -54.74) * mm, "end": v(27.76, -54.39) * mm});
            skLineSegment(sketch, "E282.MirrorCS", {"start": v(19.8, -49.01) * mm, "end": v(19.25, -48.4) * mm});
            skLineSegment(sketch, "E283.MirrorCS", {"start": v(51.18, -44.23) * mm, "end": v(52.98, -42.23) * mm});
            skArc(sketch, "E284.MirrorCS", {"start": v(44.12, -50.5) * mm, "mid": v(43.83, -48.91) * mm, "end": v(44.87, -47.67) * mm});
            skArc(sketch, "E285.MirrorCS", {"start": v(26.21, -47.14) * mm, "mid": v(27.1, -45.78) * mm, "end": v(26.62, -44.23) * mm});
            skLineSegment(sketch, "E286.MirrorCS", {"start": v(46.57, -54) * mm, "end": v(44.12, -50.5) * mm});
            skArc(sketch, "E287.MirrorCS", {"start": v(33.69, -50.5) * mm, "mid": v(33.97, -48.91) * mm, "end": v(32.93, -47.67) * mm});
            skArc(sketch, "E288.MirrorCS", {"start": v(47.31, -46.54) * mm, "mid": v(49.05, -46.54) * mm, "end": v(50.16, -47.86) * mm});
            skArc(sketch, "E289.MirrorCS", {"start": v(28.52, -54.74) * mm, "mid": v(30, -54.87) * mm, "end": v(31.24, -54) * mm});
            skArc(sketch, "E290.MirrorCS", {"start": v(30.49, -46.54) * mm, "mid": v(28.75, -46.54) * mm, "end": v(27.64, -47.86) * mm});
            skArc(sketch, "E291.MirrorCS", {"start": v(52.98, -42.23) * mm, "mid": v(54.58, -41.55) * mm, "end": v(56.12, -42.34) * mm});
            skArc(sketch, "E292.MirrorCS", {"start": v(58.65, -45.58) * mm, "mid": v(59.12, -47) * mm, "end": v(58.55, -48.4) * mm});
            skArc(sketch, "E293.MirrorCS", {"start": v(51.59, -47.14) * mm, "mid": v(50.7, -45.78) * mm, "end": v(51.18, -44.23) * mm});
            skLineSegment(sketch, "E294.MirrorCS", {"start": v(50.16, -47.86) * mm, "end": v(51.23, -51.83) * mm});
            skArc(sketch, "E295.MirrorCS", {"start": v(51.23, -51.83) * mm, "mid": v(51.1, -53.33) * mm, "end": v(50.04, -54.39) * mm});
            skLineSegment(sketch, "E296.MirrorCS", {"start": v(56.12, -42.34) * mm, "end": v(58.65, -45.58) * mm});
            skArc(sketch, "E297.MirrorCS", {"start": v(49.29, -54.74) * mm, "mid": v(47.8, -54.87) * mm, "end": v(46.57, -54) * mm});
            skLineSegment(sketch, "E298.MirrorCS", {"start": v(22.6, -49.4) * mm, "end": v(26.21, -47.14) * mm});
            skLineSegment(sketch, "E299.MirrorCS", {"start": v(21.68, -42.34) * mm, "end": v(19.15, -45.58) * mm});
            skLineSegment(sketch, "E300.MirrorCS", {"start": v(55.2, -49.4) * mm, "end": v(51.59, -47.14) * mm});
            skLineSegment(sketch, "E301.MirrorCS", {"start": v(27.64, -47.86) * mm, "end": v(26.57, -51.83) * mm});
            skLineSegment(sketch, "E302.MirrorCS", {"start": v(31.24, -54) * mm, "end": v(33.69, -50.5) * mm});
            skArc(sketch, "E303.MirrorCS", {"start": v(58, -49.01) * mm, "mid": v(56.68, -49.72) * mm, "end": v(55.2, -49.4) * mm});
            skArc(sketch, "E304.MirrorCS", {"start": v(19.15, -45.58) * mm, "mid": v(18.69, -47) * mm, "end": v(19.25, -48.4) * mm});
            skArc(sketch, "E305.MirrorCS", {"start": v(24.82, -42.23) * mm, "mid": v(23.22, -41.55) * mm, "end": v(21.68, -42.34) * mm});
            skArc(sketch, "E306.MirrorCS", {"start": v(26.57, -51.83) * mm, "mid": v(26.7, -53.33) * mm, "end": v(27.76, -54.39) * mm});
            skArc(sketch, "E307.MirrorCS", {"start": v(19.8, -49.01) * mm, "mid": v(21.13, -49.72) * mm, "end": v(22.6, -49.4) * mm});
            skPoint(sketch, "E308.orphan", {"position": v(36, -8.45) * mm});
            skPoint(sketch, "E309.orphan", {"position": v(41.8, -8.45) * mm});
            skLineSegment(sketch, "E310.MirrorCS", {"start": v(62, -40.95) * mm, "end": v(62.29, -40.17) * mm});
            skArc(sketch, "E311.MirrorCS", {"start": v(55.36, -41.62) * mm, "mid": v(54.03, -40.7) * mm, "end": v(53.9, -39.08) * mm});
            skArc(sketch, "E312.MirrorCS", {"start": v(62, -40.95) * mm, "mid": v(61.04, -42.1) * mm, "end": v(59.57, -42.36) * mm});
            skLineSegment(sketch, "E313.MirrorCS", {"start": v(59.57, -42.36) * mm, "end": v(55.36, -41.62) * mm});
            skArc(sketch, "E314.MirrorCS", {"start": v(61.33, -37.53) * mm, "mid": v(62.29, -38.68) * mm, "end": v(62.29, -40.17) * mm});
            skLineSegment(sketch, "E315.MirrorCS", {"start": v(57.77, -35.47) * mm, "end": v(61.33, -37.53) * mm});
            skLineSegment(sketch, "E316.MirrorCS", {"start": v(53.9, -39.08) * mm, "end": v(54.81, -36.55) * mm});
            skArc(sketch, "E317.MirrorCS", {"start": v(54.81, -36.55) * mm, "mid": v(56.04, -35.32) * mm, "end": v(57.77, -35.47) * mm});
            skLineSegment(sketch, "E318.MirrorCS", {"start": v(18.24, -42.36) * mm, "end": v(22.44, -41.62) * mm});
            skArc(sketch, "E319.MirrorCS", {"start": v(22.44, -41.62) * mm, "mid": v(23.77, -40.7) * mm, "end": v(23.91, -39.08) * mm});
            skLineSegment(sketch, "E320.MirrorCS", {"start": v(23.91, -39.08) * mm, "end": v(22.99, -36.55) * mm});
            skArc(sketch, "E321.MirrorCS", {"start": v(22.99, -36.55) * mm, "mid": v(21.76, -35.32) * mm, "end": v(20.04, -35.47) * mm});
            skArc(sketch, "E322.MirrorCS", {"start": v(16.48, -37.53) * mm, "mid": v(15.51, -38.68) * mm, "end": v(15.51, -40.17) * mm});
            skLineSegment(sketch, "E323.MirrorCS", {"start": v(20.04, -35.47) * mm, "end": v(16.48, -37.53) * mm});
            skArc(sketch, "E324.MirrorCS", {"start": v(15.8, -40.95) * mm, "mid": v(16.76, -42.1) * mm, "end": v(18.24, -42.36) * mm});
            skLineSegment(sketch, "E325.MirrorCS", {"start": v(15.8, -40.95) * mm, "end": v(15.51, -40.17) * mm});
            skLineSegment(sketch, "E326.MirrorCS", {"start": v(38.9, -55.83) * mm, "end": v(38.9, -12.2) * mm});
            skLineSegment(sketch, "E327.MirrorCS", {"start": v(38.9, -6.67) * mm, "end": v(38.9, -55.14) * mm});
            skLineSegment(sketch, "E328", {"start": v(-21.03, 68.23) * mm, "end": v(-23.63, 64.85) * mm});
            skLineSegment(sketch, "E329", {"start": v(-18.28, 68.84) * mm, "end": v(-17.54, 68.45) * mm});
            skLineSegment(sketch, "E330", {"start": v(-23, 61.98) * mm, "end": v(-20.62, 60.73) * mm});
            skLineSegment(sketch, "E331", {"start": v(-17.71, 61.93) * mm, "end": v(-16.47, 65.85) * mm});
            skArc(sketch, "E332.filletArc", {"start": v(-16.47, 65.85) * mm, "mid": v(-16.53, 67.34) * mm, "end": v(-17.54, 68.45) * mm});
            skArc(sketch, "E333.filletArc", {"start": v(-18.28, 68.84) * mm, "mid": v(-19.76, 69.03) * mm, "end": v(-21.03, 68.23) * mm});
            skArc(sketch, "E334.filletArc", {"start": v(-23.63, 64.85) * mm, "mid": v(-23.99, 63.26) * mm, "end": v(-23, 61.98) * mm});
            skArc(sketch, "E335.filletArc", {"start": v(-20.62, 60.73) * mm, "mid": v(-18.89, 60.65) * mm, "end": v(-17.71, 61.93) * mm});
            skLineSegment(sketch, "E336", {"start": v(41.52, -54.45) * mm, "end": v(42.26, -50.24) * mm});
            skLineSegment(sketch, "E337", {"start": v(39.36, -56.26) * mm, "end": v(38.54, -56.26) * mm});
            skLineSegment(sketch, "E338", {"start": v(40.38, -48) * mm, "end": v(37.68, -48) * mm});
            skLineSegment(sketch, "E339", {"start": v(35.66, -50.4) * mm, "end": v(36.38, -54.45) * mm});
            skArc(sketch, "E340.filletArc", {"start": v(36.38, -54.45) * mm, "mid": v(37.13, -55.75) * mm, "end": v(38.54, -56.26) * mm});
            skArc(sketch, "E341.filletArc", {"start": v(39.36, -56.26) * mm, "mid": v(40.77, -55.75) * mm, "end": v(41.52, -54.45) * mm});
            skArc(sketch, "E342.filletArc", {"start": v(42.26, -50.24) * mm, "mid": v(41.84, -48.68) * mm, "end": v(40.38, -48) * mm});
            skArc(sketch, "E343.filletArc", {"start": v(37.68, -48) * mm, "mid": v(36.11, -48.73) * mm, "end": v(35.66, -50.4) * mm});
            skLineSegment(sketch, "E344", {"start": v(15.6, -33.62) * mm, "end": v(19.8, -34.36) * mm});
            skLineSegment(sketch, "E345", {"start": v(13.8, -31.46) * mm, "end": v(13.8, -30.64) * mm});
            skLineSegment(sketch, "E346", {"start": v(22.06, -32.48) * mm, "end": v(22.06, -29.79) * mm});
            skLineSegment(sketch, "E347", {"start": v(19.65, -27.76) * mm, "end": v(15.6, -28.48) * mm});
            skArc(sketch, "E348.filletArc", {"start": v(15.6, -28.48) * mm, "mid": v(14.3, -29.23) * mm, "end": v(13.8, -30.64) * mm});
            skArc(sketch, "E349.filletArc", {"start": v(13.8, -31.46) * mm, "mid": v(14.3, -32.87) * mm, "end": v(15.6, -33.62) * mm});
            skArc(sketch, "E350.filletArc", {"start": v(19.8, -34.36) * mm, "mid": v(21.37, -33.95) * mm, "end": v(22.06, -32.48) * mm});
            skArc(sketch, "E351.filletArc", {"start": v(22.06, -29.79) * mm, "mid": v(21.32, -28.21) * mm, "end": v(19.65, -27.76) * mm});
            skPoint(sketch, "E352.orphan", {"position": v(55.73, -29.55) * mm});
            skLineSegment(sketch, "E353", {"start": v(62.2, -28.64) * mm, "end": v(57.98, -27.9) * mm});
            skLineSegment(sketch, "E354", {"start": v(64, -30.8) * mm, "end": v(64, -31.62) * mm});
            skLineSegment(sketch, "E355", {"start": v(55.73, -29.78) * mm, "end": v(55.73, -32.47) * mm});
            skLineSegment(sketch, "E356", {"start": v(58.14, -34.5) * mm, "end": v(62.2, -33.78) * mm});
            skArc(sketch, "E357.filletArc", {"start": v(62.2, -33.78) * mm, "mid": v(63.49, -33.03) * mm, "end": v(64, -31.62) * mm});
            skArc(sketch, "E358.filletArc", {"start": v(64, -30.8) * mm, "mid": v(63.49, -29.39) * mm, "end": v(62.2, -28.64) * mm});
            skArc(sketch, "E359.filletArc", {"start": v(57.98, -27.9) * mm, "mid": v(56.42, -28.31) * mm, "end": v(55.73, -29.78) * mm});
            skArc(sketch, "E360.filletArc", {"start": v(55.73, -32.47) * mm, "mid": v(56.47, -34.04) * mm, "end": v(58.14, -34.5) * mm});
            skPoint(sketch, "E361.orphan", {"position": v(40.87, -15.06) * mm});
            skPoint(sketch, "E362.orphan", {"position": v(36.93, -15.06) * mm});
            skPoint(sketch, "E363.filletArc.end.orphan", {"position": v(41.7, -12.5) * mm});
            skPoint(sketch, "E364.orphan", {"position": v(36.81, -8.48) * mm});
            skPoint(sketch, "E365.orphan", {"position": v(41, -8.48) * mm});
            skLineSegment(sketch, "E366.trimOffspring", {"start": v(38.9, -12.2) * mm, "end": v(38.9, -55.14) * mm});
            skPoint(sketch, "E367.MirrorCS.start.orphan", {"position": v(39.63, -6.67) * mm});
            skPoint(sketch, "E368.start.orphan", {"position": v(38.17, -6.67) * mm});
            skPoint(sketch, "E369.end.orphan", {"position": v(39.55, -15.06) * mm});
            skPoint(sketch, "E370.end.orphan", {"position": v(38.9, -7.37) * mm});
            skPoint(sketch, "E370.start.orphan", {"position": v(38.9, -6.67) * mm});
            skLineSegment(sketch, "E371", {"start": v(36.18, -8.01) * mm, "end": v(35.8, -12.27) * mm});
            skLineSegment(sketch, "E372", {"start": v(38.17, -6.02) * mm, "end": v(39, -5.95) * mm});
            skLineSegment(sketch, "E373", {"start": v(37.88, -14.34) * mm, "end": v(40.57, -14.1) * mm});
            skLineSegment(sketch, "E374", {"start": v(42.37, -11.53) * mm, "end": v(41.3, -7.56) * mm});
            skArc(sketch, "E375.filletArc", {"start": v(41.3, -7.56) * mm, "mid": v(40.45, -6.33) * mm, "end": v(39, -5.95) * mm});
            skArc(sketch, "E376.filletArc", {"start": v(38.17, -6.02) * mm, "mid": v(36.81, -6.65) * mm, "end": v(36.18, -8.01) * mm});
            skArc(sketch, "E377.filletArc", {"start": v(35.8, -12.27) * mm, "mid": v(36.36, -13.79) * mm, "end": v(37.88, -14.34) * mm});
            skArc(sketch, "E378.MirrorCS", {"start": v(40.57, -14.1) * mm, "mid": v(42.07, -13.24) * mm, "end": v(42.37, -11.53) * mm});
            skSolve(sketch);
        }
        {
            var Q0;
            Q0 = qSketchRegion(id + "F0", true);
            extrude(context, id + "F1", {"entities" : qUnion([Q0]), "depth" : 25.4 * mm});
        }
        {
            var Q0;
            Q0 = qSketchRegion(id + "F0", true);
            extrude(context, id + "F2", {"entities" : qUnion([Q0]), "depth" : 12.7 * mm});
        }
        {
            var Q0;
            Q0=makeQuery(id+"F1.opExtrude","SWEPT_BODY",BODY,{"disambiguationData":[OSD([sQuery(id+"F0.wireOp",EDGE,"E3"),sQuery(id+"F0.wireOp",EDGE,"10c5102c-0613-4fc7-a6b3-00d8496ef849"),sQuery(id+"F0.wireOp",EDGE,"E239.filletArc"),sQuery(id+"F0.wireOp",EDGE,"E249.MirrorCS"),sQuery(id+"F0.wireOp",EDGE,"E252.MirrorCS"),sQuery(id+"F0.wireOp",EDGE,"E254.MirrorCS"),sQuery(id+"F0.wireOp",EDGE,"E259.MirrorCS"),sQuery(id+"F0.wireOp",EDGE,"E262.MirrorCS"),sQuery(id+"F0.wireOp",EDGE,"E244.filletArc"),sQuery(id+"F0.wireOp",EDGE,"E226.filletArc"),sQuery(id+"F0.wireOp",EDGE,"E255.MirrorCS"),sQuery(id+"F0.wireOp",EDGE,"E234.filletArc"),sQuery(id+"F0.wireOp",EDGE,"E236.filletArc"),sQuery(id+"F0.wireOp",EDGE,"E265.MirrorCS"),sQuery(id+"F0.wireOp",EDGE,"E261.MirrorCS"),sQuery(id+"F0.wireOp",EDGE,"E229.filletArc"),sQuery(id+"F0.wireOp",EDGE,"E223"),sQuery(id+"F0.wireOp",EDGE,"E256.MirrorCS"),sQuery(id+"F0.wireOp",EDGE,"E227.filletArc"),sQuery(id+"F0.wireOp",EDGE,"E253.MirrorCS"),sQuery(id+"F0.wireOp",EDGE,"E245.filletArc"),sQuery(id+"F0.wireOp",EDGE,"E241"),sQuery(id+"F0.wireOp",EDGE,"E248.MirrorCS"),sQuery(id+"F0.wireOp",EDGE,"E235.filletArc"),sQuery(id+"F0.wireOp",EDGE,"E231"),sQuery(id+"F0.wireOp",EDGE,"E228.filletArc"),sQuery(id+"F0.wireOp",EDGE,"E271.MirrorCS"),sQuery(id+"F0.wireOp",EDGE,"E266.MirrorCS"),sQuery(id+"F0.wireOp",EDGE,"E263.MirrorCS"),sQuery(id+"F0.wireOp",EDGE,"E225"),sQuery(id+"F0.wireOp",EDGE,"E240"),sQuery(id+"F0.wireOp",EDGE,"E273.MirrorCS"),sQuery(id+"F0.wireOp",EDGE,"E264.MirrorCS"),sQuery(id+"F0.wireOp",EDGE,"E274.MirrorCS"),sQuery(id+"F0.wireOp",EDGE,"E270.MirrorCS"),sQuery(id+"F0.wireOp",EDGE,"E246.filletArc"),sQuery(id+"F0.wireOp",EDGE,"E258.MirrorCS"),sQuery(id+"F0.wireOp",EDGE,"E260.MirrorCS"),sQuery(id+"F0.wireOp",EDGE,"E269.MirrorCS"),sQuery(id+"F0.wireOp",EDGE,"E268.MirrorCS"),sQuery(id+"F0.wireOp",EDGE,"E237.filletArc"),sQuery(id+"F0.wireOp",EDGE,"E267.MirrorCS"),sQuery(id+"F0.wireOp",EDGE,"E222"),sQuery(id+"F0.wireOp",EDGE,"E233"),sQuery(id+"F0.wireOp",EDGE,"E230"),sQuery(id+"F0.wireOp",EDGE,"E281.MirrorCS"),sQuery(id+"F0.wireOp",EDGE,"E289.MirrorCS"),sQuery(id+"F0.wireOp",EDGE,"E290.MirrorCS"),sQuery(id+"F0.wireOp",EDGE,"E284.MirrorCS"),sQuery(id+"F0.wireOp",EDGE,"E287.MirrorCS"),sQuery(id+"F0.wireOp",EDGE,"E302.MirrorCS"),sQuery(id+"F0.wireOp",EDGE,"E297.MirrorCS"),sQuery(id+"F0.wireOp",EDGE,"E279.MirrorCS"),sQuery(id+"F0.wireOp",EDGE,"E286.MirrorCS"),sQuery(id+"F0.wireOp",EDGE,"E288.MirrorCS"),sQuery(id+"F0.wireOp",EDGE,"E310.MirrorCS"),sQuery(id+"F0.wireOp",EDGE,"E313.MirrorCS"),sQuery(id+"F0.wireOp",EDGE,"E291.MirrorCS"),sQuery(id+"F0.wireOp",EDGE,"E277.MirrorCS"),sQuery(id+"F0.wireOp",EDGE,"E295.MirrorCS"),sQuery(id+"F0.wireOp",EDGE,"E303.MirrorCS"),sQuery(id+"F0.wireOp",EDGE,"E294.MirrorCS"),sQuery(id+"F0.wireOp",EDGE,"E293.MirrorCS"),sQuery(id+"F0.wireOp",EDGE,"E292.MirrorCS"),sQuery(id+"F0.wireOp",EDGE,"E312.MirrorCS"),sQuery(id+"F0.wireOp",EDGE,"E296.MirrorCS"),sQuery(id+"F0.wireOp",EDGE,"E300.MirrorCS"),sQuery(id+"F0.wireOp",EDGE,"E311.MirrorCS"),sQuery(id+"F0.wireOp",EDGE,"E314.MirrorCS"),sQuery(id+"F0.wireOp",EDGE,"E285.MirrorCS"),sQuery(id+"F0.wireOp",EDGE,"E304.MirrorCS"),sQuery(id+"F0.wireOp",EDGE,"E299.MirrorCS"),sQuery(id+"F0.wireOp",EDGE,"E305.MirrorCS"),sQuery(id+"F0.wireOp",EDGE,"E298.MirrorCS"),sQuery(id+"F0.wireOp",EDGE,"E307.MirrorCS"),sQuery(id+"F0.wireOp",EDGE,"E301.MirrorCS"),sQuery(id+"F0.wireOp",EDGE,"E282.MirrorCS"),sQuery(id+"F0.wireOp",EDGE,"E306.MirrorCS"),sQuery(id+"F0.wireOp",EDGE,"E318.MirrorCS"),sQuery(id+"F0.wireOp",EDGE,"E319.MirrorCS"),sQuery(id+"F0.wireOp",EDGE,"E321.MirrorCS"),sQuery(id+"F0.wireOp",EDGE,"E322.MirrorCS"),sQuery(id+"F0.wireOp",EDGE,"E323.MirrorCS"),sQuery(id+"F0.wireOp",EDGE,"E324.MirrorCS"),sQuery(id+"F0.wireOp",EDGE,"E325.MirrorCS"),sQuery(id+"F0.wireOp",EDGE,"E243"),sQuery(id+"F0.wireOp",EDGE,"E247.filletArc"),sQuery(id+"F0.wireOp",EDGE,"E317.MirrorCS"),sQuery(id+"F0.wireOp",EDGE,"E2"),sQuery(id+"F0.wireOp",EDGE,"E315.MirrorCS"),sQuery(id+"F0.wireOp",EDGE,"E336"),sQuery(id+"F0.wireOp",EDGE,"E337"),sQuery(id+"F0.wireOp",EDGE,"E339"),sQuery(id+"F0.wireOp",EDGE,"E340.filletArc"),sQuery(id+"F0.wireOp",EDGE,"E341.filletArc"),sQuery(id+"F0.wireOp",EDGE,"E342.filletArc"),sQuery(id+"F0.wireOp",EDGE,"E343.filletArc"),sQuery(id+"F0.wireOp",EDGE,"E344"),sQuery(id+"F0.wireOp",EDGE,"E345"),sQuery(id+"F0.wireOp",EDGE,"E347"),sQuery(id+"F0.wireOp",EDGE,"E348.filletArc"),sQuery(id+"F0.wireOp",EDGE,"E349.filletArc"),sQuery(id+"F0.wireOp",EDGE,"E350.filletArc"),sQuery(id+"F0.wireOp",EDGE,"E351.filletArc"),sQuery(id+"F0.wireOp",EDGE,"E353"),sQuery(id+"F0.wireOp",EDGE,"E354"),sQuery(id+"F0.wireOp",EDGE,"E356"),sQuery(id+"F0.wireOp",EDGE,"E357.filletArc"),sQuery(id+"F0.wireOp",EDGE,"E358.filletArc"),sQuery(id+"F0.wireOp",EDGE,"E359.filletArc"),sQuery(id+"F0.wireOp",EDGE,"E360.filletArc")])]});
            deleteBodies(context, id + "F3", {"entities" : qUnion([Q0])});
        }
    });
